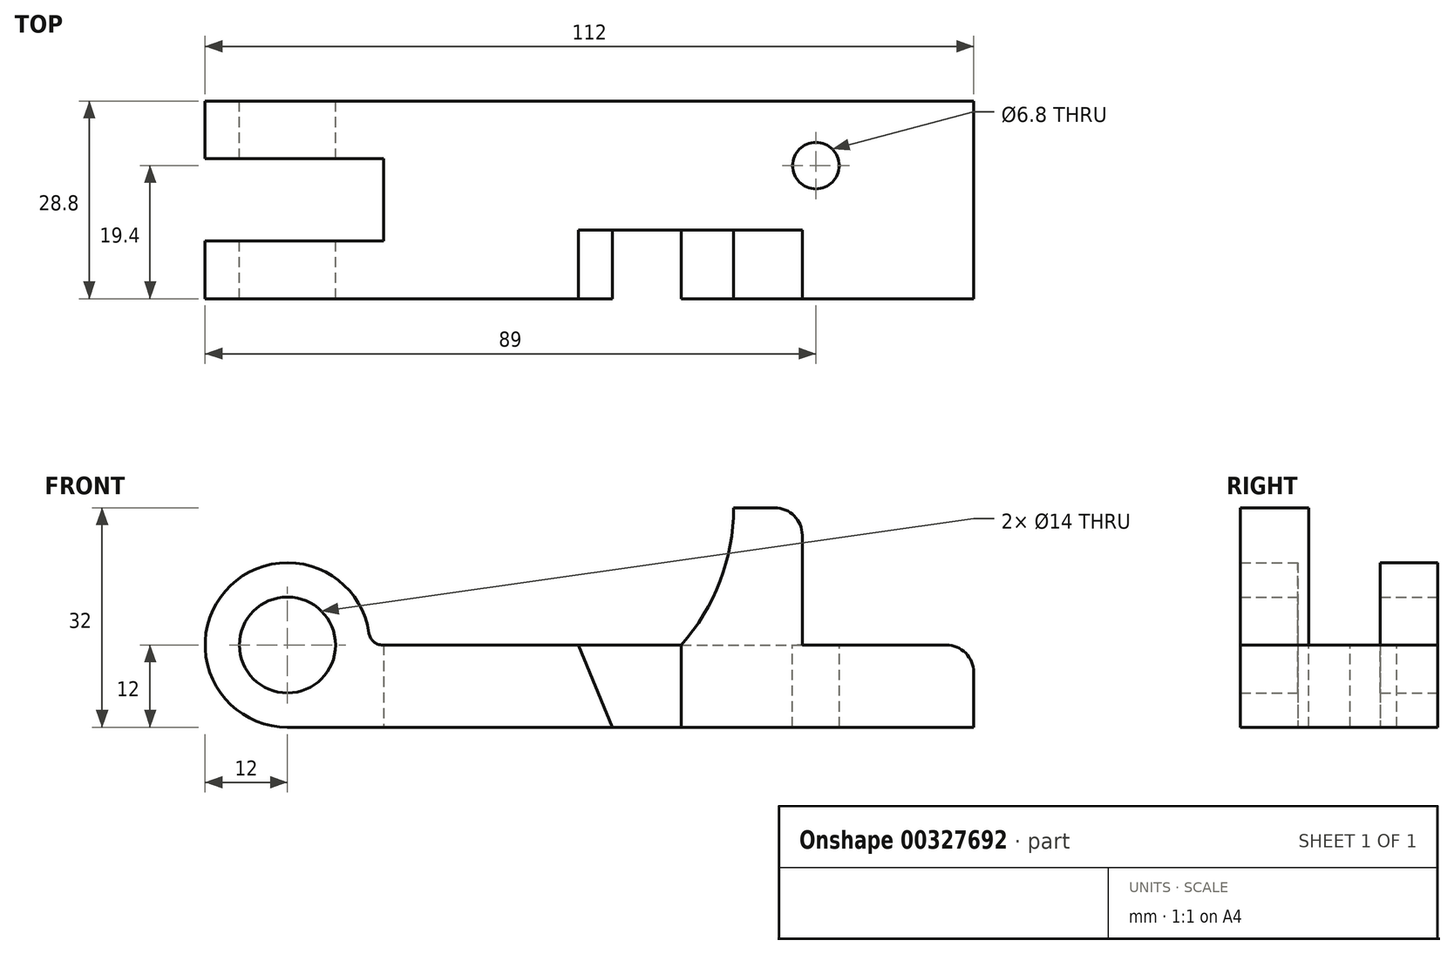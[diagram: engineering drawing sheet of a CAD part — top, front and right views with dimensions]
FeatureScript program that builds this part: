
annotation { "Feature Type Name" : "Feature", "Feature Type Description" : "" }
export const myFeature = defineFeature(function(context is Context, id is Id, definition is map)
    precondition{}
    {
        {
            var Q0;
            Q0=qCreatedBy(makeId("Front.planeOp"),FACE);
            var sketch = newSketch(context, id + "F0", { "sketchPlane" : qUnion([Q0])});
            skArc(sketch, "E0", {"start": v(12, 0) * mm, "mid": v(-8.49, 8.49) * mm, "end": v(0, -12) * mm});
            skCircle(sketch, "E1", {"center": v(0, 0) * mm, "radius": 7 * mm});
            skLineSegment(sketch, "E2.bottom", {"start": v(12, 0) * mm, "end": v(100, 0) * mm});
            skLineSegment(sketch, "E2.top", {"start": v(0, -12) * mm, "end": v(100, -12) * mm});
            skLineSegment(sketch, "E2.right", {"start": v(100, 0) * mm, "end": v(100, -12) * mm});
            skSolve(sketch);
        }
        {
            var Q0;
            Q0=makeQuery(id+"F0.imprint","IMPRINT",FACE,{"disambiguationData":[TD([[makeQuery(id+"F0.imprint","IMPRINT",EDGE,{"derivedFrom":sQuery(id+"F0.wireOp",EDGE,"E0")}),1.0]])]});
            extrude(context, id + "F1", {"entities" : qUnion([Q0]), "depth" : 28.8 * mm});
        }
        {
            var Q0;
            Q0=makeQuery(id+"F1.opExtrude","CAP_FACE",FACE,{"disambiguationData":[OSD([sQuery(id+"F0.wireOp",EDGE,"E0"),sQuery(id+"F0.wireOp",EDGE,"E1"),sQuery(id+"F0.wireOp",EDGE,"E2.bottom"),sQuery(id+"F0.wireOp",EDGE,"E2.top"),sQuery(id+"F0.wireOp",EDGE,"E2.right")])],"isStart":false});
            cPlane(context, id + "F2", {"entities" : qUnion([Q0]), "cplaneType" : CPlaneType.OFFSET, "offset" : 8.4 * mm, "oppositeDirection" : true, "width" : 150 * mm, "height" : 150 * mm});
        }
        {
            var Q0;
            Q0=qCreatedBy(id+"F2.planeOp",FACE);
            var sketch = newSketch(context, id + "F3", { "sketchPlane" : qUnion([Q0])});
            skLineSegment(sketch, "E3.right", {"start": v(14, 0) * mm, "end": v(14, -12) * mm});
            skLineSegment(sketch, "E4.0", {"start": v(12, 0) * mm, "end": v(14, 0) * mm});
            skLineSegment(sketch, "E5.0", {"start": v(0, -12) * mm, "end": v(14, -12) * mm});
            skArc(sketch, "E6.0", {"start": v(12, 0) * mm, "mid": v(-8.49, 8.49) * mm, "end": v(0, -12) * mm});
            skPoint(sketch, "E7.orphan", {"position": v(100, 0) * mm});
            skPoint(sketch, "E8.orphan", {"position": v(100, -12) * mm});
            skSolve(sketch);
        }
        {
            var Q0;
            Q0=makeQuery(id+"F3.imprint","IMPRINT",FACE,{"disambiguationData":[TD([[makeQuery(id+"F3.imprint","IMPRINT",EDGE,{"derivedFrom":sQuery(id+"F3.wireOp",EDGE,"E3.right")}),-1.0]])]});
            extrude(context, id + "F4", {"entities" : qUnion([Q0]), "operationType" : NewBodyOperationType.REMOVE, "oppositeDirection" : true, "depth" : 12 * mm});
        }
        {
            var Q0;
            Q0=makeQuery(id+"F1.opExtrude","CAP_FACE",FACE,{"disambiguationData":[OSD([sQuery(id+"F0.wireOp",EDGE,"E0"),sQuery(id+"F0.wireOp",EDGE,"E1"),sQuery(id+"F0.wireOp",EDGE,"E2.bottom"),sQuery(id+"F0.wireOp",EDGE,"E2.top"),sQuery(id+"F0.wireOp",EDGE,"E2.right")])],"isStart":false});
            var sketch = newSketch(context, id + "F5", { "sketchPlane" : qUnion([Q0])});
            skLineSegment(sketch, "E9.bottom", {"start": v(65, 0) * mm, "end": v(75, 0) * mm});
            skLineSegment(sketch, "E9.top", {"start": v(65, 20) * mm, "end": v(75, 20) * mm});
            skLineSegment(sketch, "E9.left", {"start": v(65, 0) * mm, "end": v(65, 20) * mm, "construction": true});
            skLineSegment(sketch, "E9.right", {"start": v(75, 0) * mm, "end": v(75, 20) * mm});
            skArc(sketch, "E10", {"start": v(57.36, 0) * mm, "mid": v(63.02, 9.3) * mm, "end": v(65, 20) * mm});
            skLineSegment(sketch, "E11", {"start": v(57.36, 0) * mm, "end": v(57.36, -12) * mm});
            skLineSegment(sketch, "E12", {"start": v(57.36, 0) * mm, "end": v(65, 0) * mm});
            skSolve(sketch);
        }
        {
            var Q0;
            Q0=makeQuery(id+"F5.imprint","IMPRINT",FACE,{"disambiguationData":[TD([[makeQuery(id+"F5.imprint","IMPRINT",EDGE,{"derivedFrom":sQuery(id+"F5.wireOp",EDGE,"E9.bottom")}),1.0]])]});
            extrude(context, id + "F6", {"entities" : qUnion([Q0]), "operationType" : NewBodyOperationType.ADD, "oppositeDirection" : true, "depth" : 10 * mm});
        }
        {
            var Q0;
            Q0=makeQuery(id+"F6.boolean.opBoolean","MERGE",FACE,{"derivedFrom":[makeQuery(id+"F1.opExtrude","CAP_FACE",FACE,{"disambiguationData":[OSD([sQuery(id+"F0.wireOp",EDGE,"E0"),sQuery(id+"F0.wireOp",EDGE,"E1"),sQuery(id+"F0.wireOp",EDGE,"E2.bottom"),sQuery(id+"F0.wireOp",EDGE,"E2.top"),sQuery(id+"F0.wireOp",EDGE,"E2.right")])],"isStart":false}),makeQuery(id+"F6.opExtrude","CAP_FACE",FACE,{"disambiguationData":[OSD([sQuery(id+"F5.wireOp",EDGE,"E9.bottom"),sQuery(id+"F5.wireOp",EDGE,"E9.top"),sQuery(id+"F5.wireOp",EDGE,"E9.right"),sQuery(id+"F5.wireOp",EDGE,"E10"),sQuery(id+"F5.wireOp",EDGE,"E12")])],"isStart":true})]});
            var sketch = newSketch(context, id + "F7", { "sketchPlane" : qUnion([Q0])});
            skLineSegment(sketch, "E13", {"start": v(57.36, 0) * mm, "end": v(57.36, -12) * mm});
            skLineSegment(sketch, "E14", {"start": v(42.36, 0) * mm, "end": v(47.36, -12) * mm});
            skLineSegment(sketch, "E15", {"start": v(42.36, 0) * mm, "end": v(57.36, 0) * mm});
            skLineSegment(sketch, "E16", {"start": v(57.36, -12) * mm, "end": v(47.36, -12) * mm});
            skSolve(sketch);
        }
        {
            var Q0;
            Q0=makeQuery(id+"F7.imprint","IMPRINT",FACE,{"disambiguationData":[TD([[makeQuery(id+"F7.imprint","IMPRINT",EDGE,{"derivedFrom":sQuery(id+"F7.wireOp",EDGE,"E13")}),-1.0]])]});
            var Q1;
            Q1=makeQuery(id+"F6.opExtrude","CAP_FACE",FACE,{"disambiguationData":[OSD([sQuery(id+"F5.wireOp",EDGE,"E9.bottom"),sQuery(id+"F5.wireOp",EDGE,"E9.top"),sQuery(id+"F5.wireOp",EDGE,"E9.right"),sQuery(id+"F5.wireOp",EDGE,"E10"),sQuery(id+"F5.wireOp",EDGE,"E12")])],"isStart":false});
            extrude(context, id + "F8", {"entities" : qUnion([Q0]), "operationType" : NewBodyOperationType.REMOVE, "endBound" : BoundingType.UP_TO_SURFACE, "oppositeDirection" : true, "endBoundEntityFace" : qUnion([Q1]), "depth" : 25 * mm});
        }
        {
            var Q0;
            Q0=makeQuery(id+"F1.opExtrude","SWEPT_FACE",FACE,{"disambiguationData":[OSD([sQuery(id+"F0.wireOp",EDGE,"E2.bottom")])]});
            var sketch = newSketch(context, id + "F9", { "sketchPlane" : qUnion([Q0])});
            skCircle(sketch, "E17", {"center": v(77, -9.4) * mm, "radius": 3.4 * mm});
            skLineSegment(sketch, "E18.0", {"start": v(57.36, -18.8) * mm, "end": v(42.36, -18.8) * mm});
            skLineSegment(sketch, "E19", {"start": v(75, -18.8) * mm, "end": v(75, 0) * mm, "construction": true});
            skPoint(sketch, "E20", {"position": v(75, -9.4) * mm});
            skSolve(sketch);
        }
        {
            var Q0;
            Q0=makeQuery(id+"F9.imprint","IMPRINT",FACE,{"disambiguationData":[TD([[makeQuery(id+"F9.imprint","IMPRINT",EDGE,{"derivedFrom":sQuery(id+"F9.wireOp",EDGE,"E17")}),1.0]])]});
            extrude(context, id + "F10", {"entities" : qUnion([Q0]), "operationType" : NewBodyOperationType.REMOVE, "endBound" : BoundingType.UP_TO_NEXT, "oppositeDirection" : true, "depth" : 25 * mm});
        }
        {
            var Q0;
            Q0=makeQuery(id+"F6.opExtrude","SWEPT_EDGE",EDGE,{"disambiguationData":[OSD([sQuery(id+"F0.wireOp",EDGE,"E2.bottom"),sQuery(id+"F5.wireOp",EDGE,"E9.bottom"),sQuery(id+"F5.wireOp",EDGE,"E9.right")])]});
            var Q1;
            {var subQ0=sQuery(id+"F0.wireOp",EDGE,"E0");var subQ1=sQuery(id+"F0.wireOp",EDGE,"E2.bottom");Q1=makeQuery(id+"F4.boolean.opBoolean","SPLIT",EDGE,{"disambiguationData":[TD([makeQuery(id+"F4.opExtrude","CAP_FACE",FACE,{"disambiguationData":[OSD([sQuery(id+"F3.wireOp",EDGE,"E3.right"),sQuery(id+"F3.wireOp",EDGE,"E4.0"),sQuery(id+"F3.wireOp",EDGE,"E5.0"),sQuery(id+"F3.wireOp",EDGE,"E6.0")])],"isStart":true})])],"derivedFrom":makeQuery(id+"F1.opExtrude","SWEPT_EDGE",EDGE,{"disambiguationData":[OSD([subQ0,subQ1])]})});}
            var Q2;
            {var subQ0=sQuery(id+"F0.wireOp",EDGE,"E0");var subQ1=sQuery(id+"F0.wireOp",EDGE,"E2.bottom");Q2=makeQuery(id+"F4.boolean.opBoolean","SPLIT",EDGE,{"disambiguationData":[TD([makeQuery(id+"F4.opExtrude","CAP_FACE",FACE,{"disambiguationData":[OSD([sQuery(id+"F3.wireOp",EDGE,"E3.right"),sQuery(id+"F3.wireOp",EDGE,"E4.0"),sQuery(id+"F3.wireOp",EDGE,"E5.0"),sQuery(id+"F3.wireOp",EDGE,"E6.0")])],"isStart":false})])],"derivedFrom":makeQuery(id+"F1.opExtrude","SWEPT_EDGE",EDGE,{"disambiguationData":[OSD([subQ0,subQ1])]})});}
            fillet(context, id + "F11", {"entities" : qUnion([Q0, Q1, Q2]), "radius" : 2 * mm, "tangentPropagation" : true, "allowEdgeOverflow" : false});
        }
        {
            var Q0;
            Q0=makeQuery(id+"F6.opExtrude","SWEPT_EDGE",EDGE,{"disambiguationData":[OSD([sQuery(id+"F5.wireOp",EDGE,"E9.top"),sQuery(id+"F5.wireOp",EDGE,"E9.right")])]});
            var Q1;
            Q1=makeQuery(id+"F1.opExtrude","SWEPT_EDGE",EDGE,{"disambiguationData":[OSD([sQuery(id+"F0.wireOp",EDGE,"E2.bottom"),sQuery(id+"F0.wireOp",EDGE,"E2.right")])]});
            fillet(context, id + "F12", {"entities" : qUnion([Q0, Q1]), "radius" : 4 * mm, "tangentPropagation" : true, "allowEdgeOverflow" : false});
        }
    });
